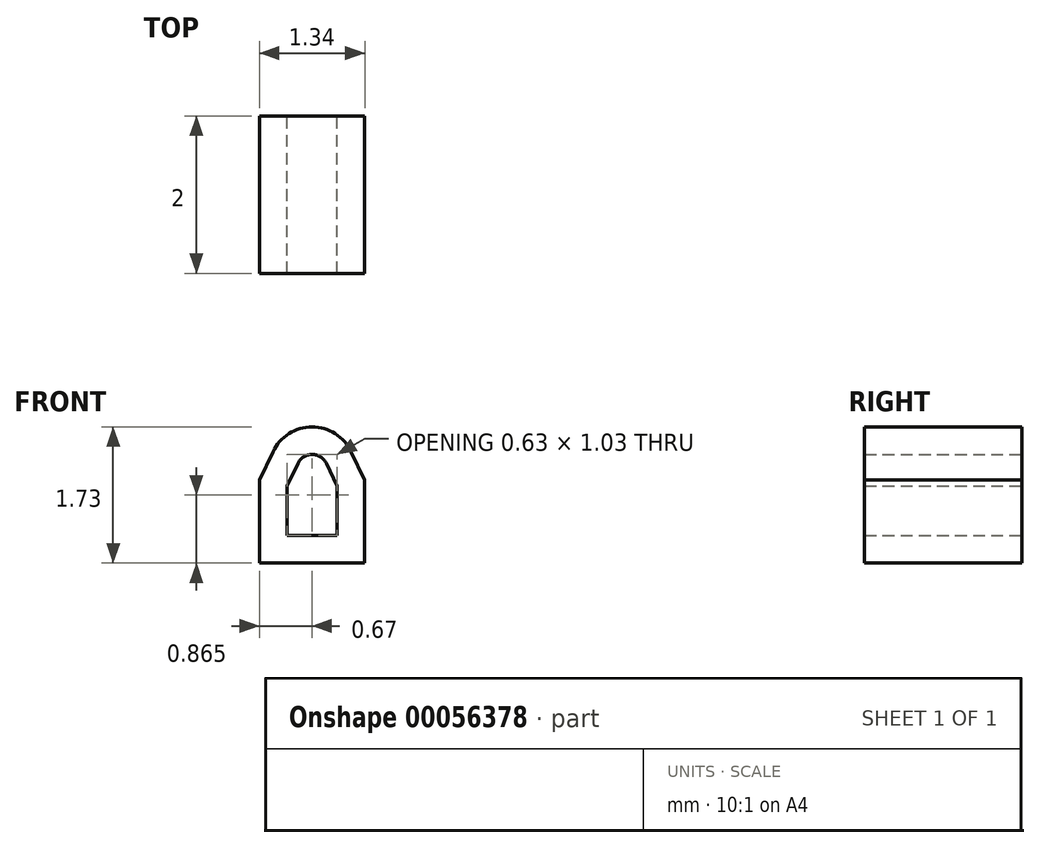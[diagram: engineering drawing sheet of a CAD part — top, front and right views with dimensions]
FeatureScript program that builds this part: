
annotation { "Feature Type Name" : "Feature", "Feature Type Description" : "" }
export const myFeature = defineFeature(function(context is Context, id is Id, definition is map)
    precondition{}
    {
        {
            var Q0;
            Q0=qCreatedBy(makeId("Front.planeOp"),FACE);
            var sketch = newSketch(context, id + "F0", { "sketchPlane" : qUnion([Q0])});
            skLineSegment(sketch, "E0", {"start": v(-0.32, -0.2) * mm, "end": v(0.31, -0.2) * mm});
            skLineSegment(sketch, "E1", {"start": v(-0.32, -0.2) * mm, "end": v(-0.32, 0.43) * mm});
            skLineSegment(sketch, "E2", {"start": v(0.31, -0.2) * mm, "end": v(0.31, 0.43) * mm});
            skLineSegment(sketch, "E3", {"start": v(0, 0) * mm, "end": v(0, -1.9) * mm, "construction": true});
            skLineSegment(sketch, "E4", {"start": v(-0.32, 0.43) * mm, "end": v(0.31, 0.43) * mm, "construction": true});
            skLineSegment(sketch, "E5", {"start": v(0, 0.43) * mm, "end": v(0, 0.63) * mm, "construction": true});
            skPoint(sketch, "E5.endSnap0", {"position": v(0, 0.43) * mm});
            skLineSegment(sketch, "E6", {"start": v(-0.31, 0.43) * mm, "end": v(-0.18, 0.72) * mm});
            skLineSegment(sketch, "E7", {"start": v(0.31, 0.43) * mm, "end": v(0.18, 0.72) * mm});
            skArc(sketch, "E8", {"start": v(-0.18, 0.72) * mm, "mid": v(0, 0.83) * mm, "end": v(0.18, 0.72) * mm});
            skLineSegment(sketch, "E9.0", {"start": v(-0.67, -0.55) * mm, "end": v(-0.67, 0.5) * mm});
            skArc(sketch, "E9.1", {"start": v(-0.5, 0.86) * mm, "mid": v(0, 1.18) * mm, "end": v(0.5, 0.86) * mm});
            skLineSegment(sketch, "E9.2", {"start": v(0.67, 0.5) * mm, "end": v(0.5, 0.86) * mm});
            skLineSegment(sketch, "E9.3", {"start": v(-0.67, 0.5) * mm, "end": v(-0.5, 0.86) * mm});
            skLineSegment(sketch, "E9.4", {"start": v(0.67, -0.55) * mm, "end": v(0.67, 0.5) * mm});
            skLineSegment(sketch, "E9.5", {"start": v(-0.67, -0.55) * mm, "end": v(0.67, -0.55) * mm});
            skSolve(sketch);
        }
        {
            var Q0;
            Q0=makeQuery(id+"F0.imprint","IMPRINT",FACE,{"disambiguationData":[TD([[makeQuery(id+"F0.imprint","IMPRINT",EDGE,{"derivedFrom":sQuery(id+"F0.wireOp",EDGE,"E0")}),-1.0]])]});
            extrude(context, id + "F1", {"entities" : qUnion([Q0]), "depth" : 2 * mm});
        }
    });
